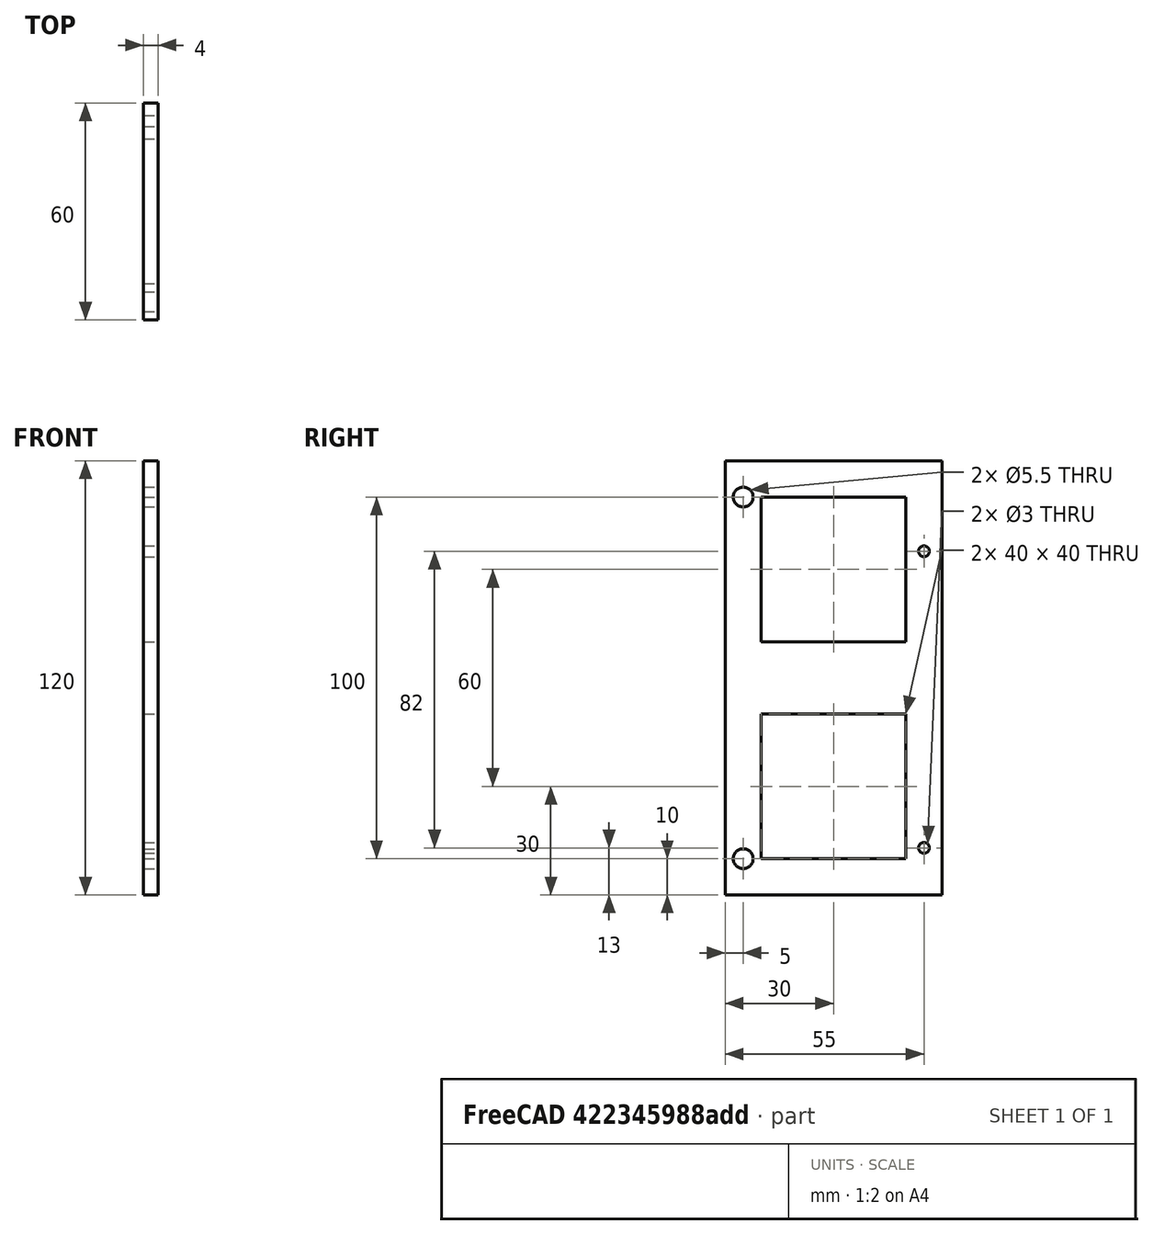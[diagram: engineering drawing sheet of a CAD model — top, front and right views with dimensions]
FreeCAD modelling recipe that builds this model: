
FCSTD DOCUMENT  (FreeCAD 0.15R4671 (Git))
Label: soporte electronica
License: All rights reserved
LicenseURL: http://es.wikipedia.org/wiki/Todos_los_derechos_reservados
objects: Part::Cylinder×4, Part::Box×3, Part::MultiFuse×2, Part::Cut×1
note: 10 computed .brp shape members not serialized (recipe doc carries the construction recipe); baked Part::Feature solids carry a one-line shape summary decoded from their .brp

FEATURE [Part::Box] Box  label="Cubo"
  Height = 120
  Length = 4
  Width = 60
FEATURE [Part::Box] Box001  label="Cubo001"
  Height = 40
  Length = 4
  Placement = pos=(0,10,10) rot=(0,0,1;0rad)
  Width = 40
FEATURE [Part::Box] Box002  label="Cubo002"
  Height = 40
  Length = 4
  Placement = pos=(0,10,70) rot=(0,0,1;0rad)
  Width = 40
FEATURE [Part::MultiFuse] Fusion
  Shapes = -> [Box001,Box002]
FEATURE [Part::Cylinder] Cylinder  label="Cilindro"
  Angle = 360
  Height = 4
  Placement = pos=(0,5,10) rot=(0,1,0;1.5708rad)
  Radius = 2.75
FEATURE [Part::Cylinder] Cylinder001  label="Cilindro001"
  Angle = 360
  Height = 4
  Placement = pos=(0,5,110) rot=(0,1,0;1.5708rad)
  Radius = 2.75
FEATURE [Part::Cylinder] Cylinder002  label="Cilindro002"
  Angle = 360
  Height = 4
  Placement = pos=(0,55,95) rot=(0,1,0;1.5708rad)
  Radius = 1.5
FEATURE [Part::Cylinder] Cylinder003  label="Cilindro003"
  Angle = 360
  Height = 4
  Placement = pos=(0,55,13) rot=(0,1,0;1.5708rad)
  Radius = 1.5
FEATURE [Part::MultiFuse] Fusion001
  Shapes = -> [Fusion,Cylinder002,Cylinder003,Cylinder,Cylinder001]
FEATURE [Part::Cut] Cut
  Base = -> Box
  Tool = -> Fusion001
